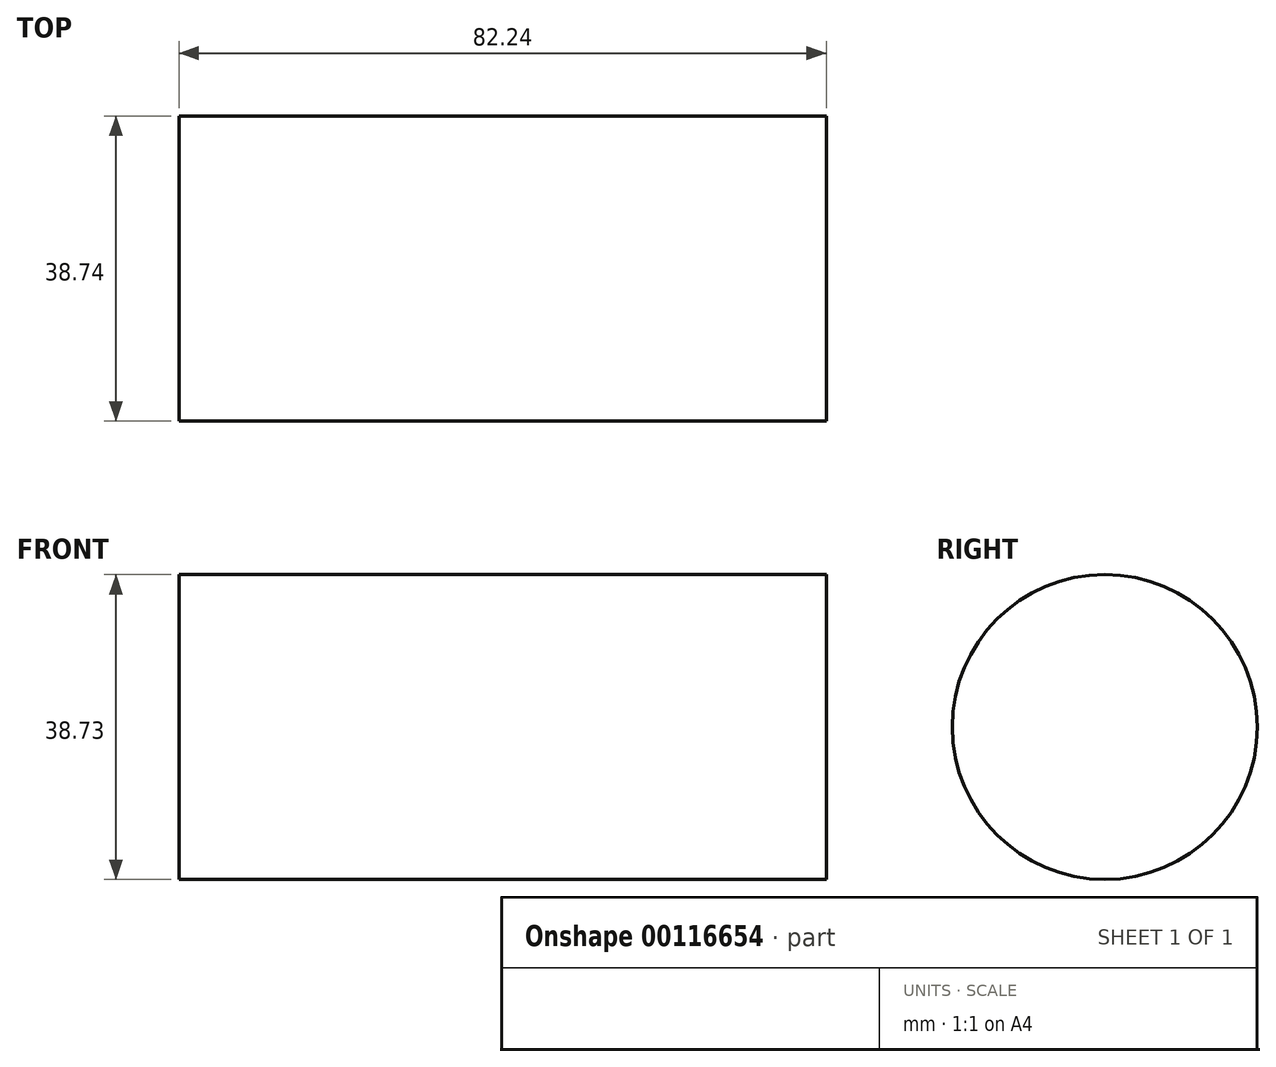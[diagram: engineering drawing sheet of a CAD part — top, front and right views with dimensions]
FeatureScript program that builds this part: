
annotation { "Feature Type Name" : "Feature", "Feature Type Description" : "" }
export const myFeature = defineFeature(function(context is Context, id is Id, definition is map)
    precondition{}
    {
        {
            var Q0;
            Q0=qCreatedBy(makeId("Front.planeOp"),FACE);
            var sketch = newSketch(context, id + "F0", { "sketchPlane" : qUnion([Q0])});
            skLineSegment(sketch, "E0.bottom", {"start": v(-41.12, 9.68) * mm, "end": v(41.12, 9.68) * mm});
            skLineSegment(sketch, "E0.top", {"start": v(-41.12, -9.68) * mm, "end": v(41.12, -9.68) * mm});
            skLineSegment(sketch, "E0.left", {"start": v(-41.12, 9.68) * mm, "end": v(-41.12, -9.68) * mm});
            skLineSegment(sketch, "E0.right", {"start": v(41.12, 9.68) * mm, "end": v(41.12, -9.68) * mm});
            skPoint(sketch, "E0.middle", {"position": v(0, 0) * mm});
            skSolve(sketch);
        }
        {
            var Q0;
            Q0 = qSketchRegion(id + "F0", true);
            var Q1;
            Q1=sQuery(id+"F0.wireOp",EDGE,"E0.bottom");
            revolve(context, id + "F1", {"entities" : qUnion([Q0]), "axis" : qUnion([Q1]), "revolveType" : RevolveType.FULL});
        }
    });
